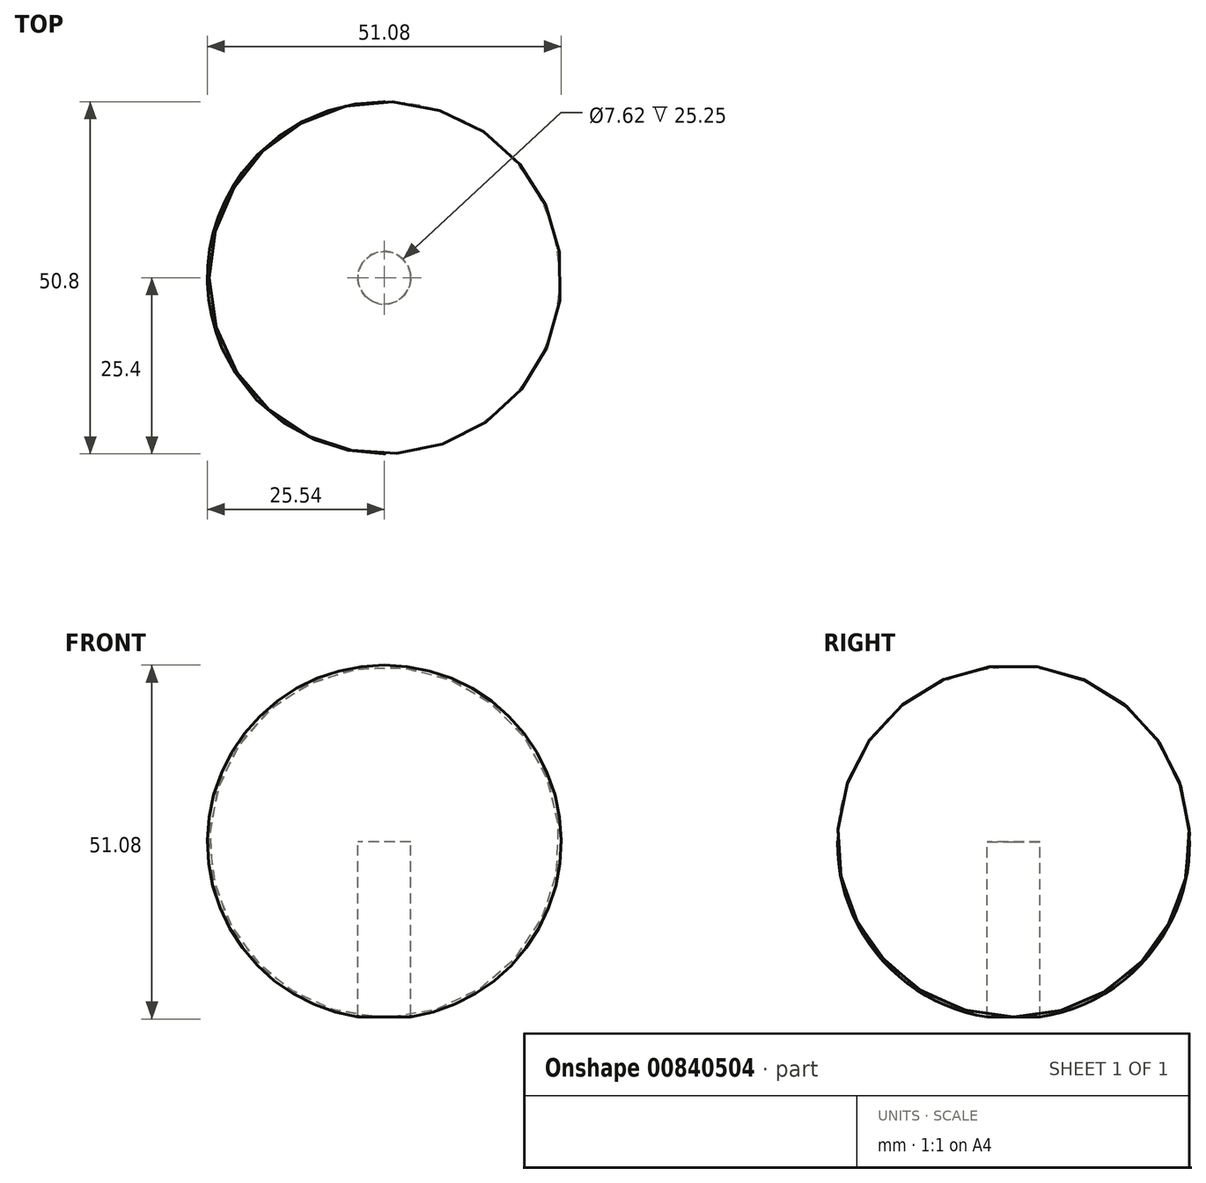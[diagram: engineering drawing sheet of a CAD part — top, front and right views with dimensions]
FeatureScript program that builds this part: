
annotation { "Feature Type Name" : "Feature", "Feature Type Description" : "" }
export const myFeature = defineFeature(function(context is Context, id is Id, definition is map)
    precondition{}
    {
        {
            var Q0;
            Q0=qCreatedBy(makeId("Top.planeOp"),FACE);
            var sketch = newSketch(context, id + "F0", { "sketchPlane" : qUnion([Q0])});
            skLineSegment(sketch, "E0", {"start": v(0, 0) * mm, "end": v(0, 50.8) * mm});
            skArc(sketch, "E1", {"start": v(0, 0) * mm, "mid": v(25.54, 25.4) * mm, "end": v(0, 50.8) * mm});
            skSolve(sketch);
        }
        {
            var Q0;
            Q0=makeQuery(id+"F0.imprint","IMPRINT",FACE,{"disambiguationData":[TD([[makeQuery(id+"F0.imprint","IMPRINT",EDGE,{"derivedFrom":sQuery(id+"F0.wireOp",EDGE,"E0")}),-1.0]])]});
            var Q1;
            Q1=sQuery(id+"F0.wireOp",EDGE,"E0");
            revolve(context, id + "F1", {"surfaceOperationType" : NewSurfaceOperationType.NEW, "entities" : qUnion([Q0]), "axis" : qUnion([Q1]), "revolveType" : RevolveType.FULL});
        }
        {
            var Q0;
            Q0=qCreatedBy(makeId("Top.planeOp"),FACE);
            var sketch = newSketch(context, id + "F2", { "sketchPlane" : qUnion([Q0])});
            skCircle(sketch, "E2", {"center": v(0, 25.4) * mm, "radius": 3.81 * mm});
            skSolve(sketch);
        }
        {
            var Q0;
            Q0 = qSketchRegion(id + "F2", true);
            extrude(context, id + "F3", {"entities" : qUnion([Q0]), "operationType" : NewBodyOperationType.REMOVE, "endBound" : BoundingType.THROUGH_ALL, "oppositeDirection" : true, "depth" : 25.4 * mm, "offsetDistance" : 25.4 * mm});
        }
    });
